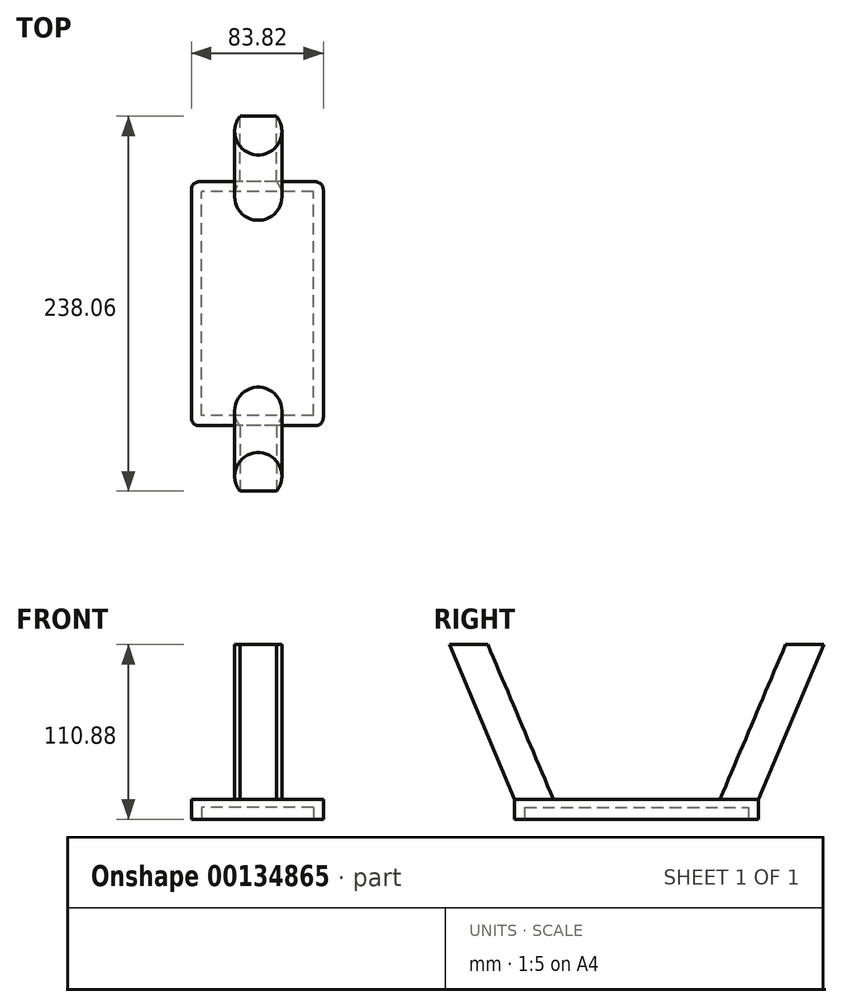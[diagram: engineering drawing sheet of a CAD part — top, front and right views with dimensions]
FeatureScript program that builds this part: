
annotation { "Feature Type Name" : "Feature", "Feature Type Description" : "" }
export const myFeature = defineFeature(function(context is Context, id is Id, definition is map)
    precondition{}
    {
        {
            var Q0;
            Q0=qCreatedBy(makeId("Top.planeOp"),FACE);
            var sketch = newSketch(context, id + "F0", { "sketchPlane" : qUnion([Q0])});
            skLineSegment(sketch, "E0.bottom", {"start": v(41.9, -77.47) * mm, "end": v(-41.91, -77.47) * mm});
            skLineSegment(sketch, "E0.top", {"start": v(41.91, 77.47) * mm, "end": v(-41.9, 77.47) * mm});
            skLineSegment(sketch, "E0.left", {"start": v(41.9, -77.47) * mm, "end": v(41.91, 77.47) * mm});
            skLineSegment(sketch, "E0.right", {"start": v(-41.91, -77.47) * mm, "end": v(-41.9, 77.47) * mm});
            skPoint(sketch, "E0.middle", {"position": v(0, 0) * mm});
            skSolve(sketch);
        }
        {
            var Q0;
            Q0=makeQuery(id+"F0.imprint","IMPRINT",FACE,{"disambiguationData":[TD([[makeQuery(id+"F0.imprint","IMPRINT",EDGE,{"derivedFrom":sQuery(id+"F0.wireOp",EDGE,"E0.bottom")}),-1.0]])]});
            extrude(context, id + "F1", {"entities" : qUnion([Q0]), "depth" : 12.7 * mm});
        }
        {
            var Q0;
            Q0=qCreatedBy(makeId("Top.planeOp"),FACE);
            var sketch = newSketch(context, id + "F2", { "sketchPlane" : qUnion([Q0])});
            skLineSegment(sketch, "E1.bottom", {"start": v(35.56, -71.12) * mm, "end": v(-35.56, -71.12) * mm});
            skLineSegment(sketch, "E1.top", {"start": v(35.56, 71.12) * mm, "end": v(-35.56, 71.12) * mm});
            skLineSegment(sketch, "E1.left", {"start": v(35.56, -71.12) * mm, "end": v(35.56, 71.12) * mm});
            skLineSegment(sketch, "E1.right", {"start": v(-35.56, -71.12) * mm, "end": v(-35.56, 71.12) * mm});
            skPoint(sketch, "E1.middle", {"position": v(0, 0) * mm});
            skSolve(sketch);
        }
        {
            var Q0;
            Q0=makeQuery(id+"F2.imprint","IMPRINT",FACE,{"disambiguationData":[TD([[makeQuery(id+"F2.imprint","IMPRINT",EDGE,{"derivedFrom":sQuery(id+"F2.wireOp",EDGE,"E1.bottom")}),-1.0]])]});
            extrude(context, id + "F3", {"entities" : qUnion([Q0]), "operationType" : NewBodyOperationType.REMOVE, "depth" : 7.62 * mm});
        }
        {
            var Q0;
            Q0=makeQuery(id+"F1.opExtrude","SWEPT_EDGE",EDGE,{"disambiguationData":[OSD([sQuery(id+"F0.wireOp",EDGE,"E0.bottom"),sQuery(id+"F0.wireOp",EDGE,"E0.left")])]});
            fillet(context, id + "F4", {"entities" : qUnion([Q0]), "radius" : 5.08 * mm, "tangentPropagation" : true, "allowEdgeOverflow" : false});
        }
        {
            var Q0;
            Q0=makeQuery(id+"F1.opExtrude","SWEPT_EDGE",EDGE,{"disambiguationData":[OSD([sQuery(id+"F0.wireOp",EDGE,"E0.top"),sQuery(id+"F0.wireOp",EDGE,"E0.left")])]});
            fillet(context, id + "F5", {"entities" : qUnion([Q0]), "radius" : 5.08 * mm, "tangentPropagation" : true, "allowEdgeOverflow" : false});
        }
        {
            var Q0;
            Q0=makeQuery(id+"F1.opExtrude","SWEPT_EDGE",EDGE,{"disambiguationData":[OSD([sQuery(id+"F0.wireOp",EDGE,"E0.bottom"),sQuery(id+"F0.wireOp",EDGE,"E0.right")])]});
            fillet(context, id + "F6", {"entities" : qUnion([Q0]), "radius" : 5.08 * mm, "tangentPropagation" : true, "allowEdgeOverflow" : false});
        }
        {
            var Q0;
            Q0=makeQuery(id+"F1.opExtrude","SWEPT_EDGE",EDGE,{"disambiguationData":[OSD([sQuery(id+"F0.wireOp",EDGE,"E0.top"),sQuery(id+"F0.wireOp",EDGE,"E0.right")])]});
            fillet(context, id + "F7", {"entities" : qUnion([Q0]), "radius" : 5.08 * mm, "tangentPropagation" : true, "allowEdgeOverflow" : false});
        }
        {
            var Q0;
            Q0=makeQuery(id+"F1.opExtrude","CAP_FACE",FACE,{"disambiguationData":[OSD([sQuery(id+"F0.wireOp",EDGE,"E0.bottom"),sQuery(id+"F0.wireOp",EDGE,"E0.top"),sQuery(id+"F0.wireOp",EDGE,"E0.left"),sQuery(id+"F0.wireOp",EDGE,"E0.right")])],"isStart":false});
            var sketch = newSketch(context, id + "F8", { "sketchPlane" : qUnion([Q0])});
            skCircle(sketch, "E2", {"center": v(0.6, -67.98) * mm, "radius": 15 * mm});
            skPoint(sketch, "E2.first.point", {"position": v(0, -82.96) * mm});
            skPoint(sketch, "E2.second.point", {"position": v(0, -52.99) * mm});
            skPoint(sketch, "E2.third.point", {"position": v(-5, -54.06) * mm});
            skSolve(sketch);
        }
        {
            var Q0;
            Q0=qCreatedBy(makeId("Right.planeOp"),FACE);
            var sketch = newSketch(context, id + "F9", { "sketchPlane" : qUnion([Q0])});
            skLineSegment(sketch, "E3", {"start": v(-68.24, 13.76) * mm, "end": v(-109.8, 111.94) * mm});
            skSolve(sketch);
        }
        {
            var Q0;
            {var subQ0=sQuery(id+"F8.wireOp",EDGE,"E2");var subQ1=makeQuery(id+"F1.opExtrude","CAP_EDGE",EDGE,{"disambiguationData":[OSD([sQuery(id+"F0.wireOp",EDGE,"E0.bottom")])],"isStart":false});var subQ2=makeQuery(id+"F8.imprint","INTERSECT",VERTEX,{"disambiguationData":[OD(0.0)],"derivedFrom":[subQ1,subQ0]});Q0=makeQuery(id+"F8.imprint","IMPRINT",FACE,{"disambiguationData":[TD([[makeQuery(id+"F8.imprint","IMPRINT",EDGE,{"disambiguationData":[TD([[subQ2,-1.0]])],"derivedFrom":subQ0}),1.0]])]});}
            var Q1;
            Q1=sQuery(id+"F9.wireOp",EDGE,"E3");
            sweep(context, id + "F10", {"operationType" : NewBodyOperationType.ADD, "profiles" : qUnion([Q0]), "path" : qUnion([Q1])});
        }
        {
            var Q0;
            Q0=makeQuery(id+"F1.opExtrude","SWEPT_BODY",BODY,{"disambiguationData":[OSD([sQuery(id+"F0.wireOp",EDGE,"E0.bottom"),sQuery(id+"F0.wireOp",EDGE,"E0.top"),sQuery(id+"F0.wireOp",EDGE,"E0.left"),sQuery(id+"F0.wireOp",EDGE,"E0.right")])]});
            var Q1;
            Q1=qCreatedBy(makeId("Front.planeOp"),FACE);
            mirror(context, id + "F11", {"operationType" : NewBodyOperationType.ADD, "entities" : qUnion([Q0]), "mirrorPlane" : qUnion([Q1])});
        }
    });
